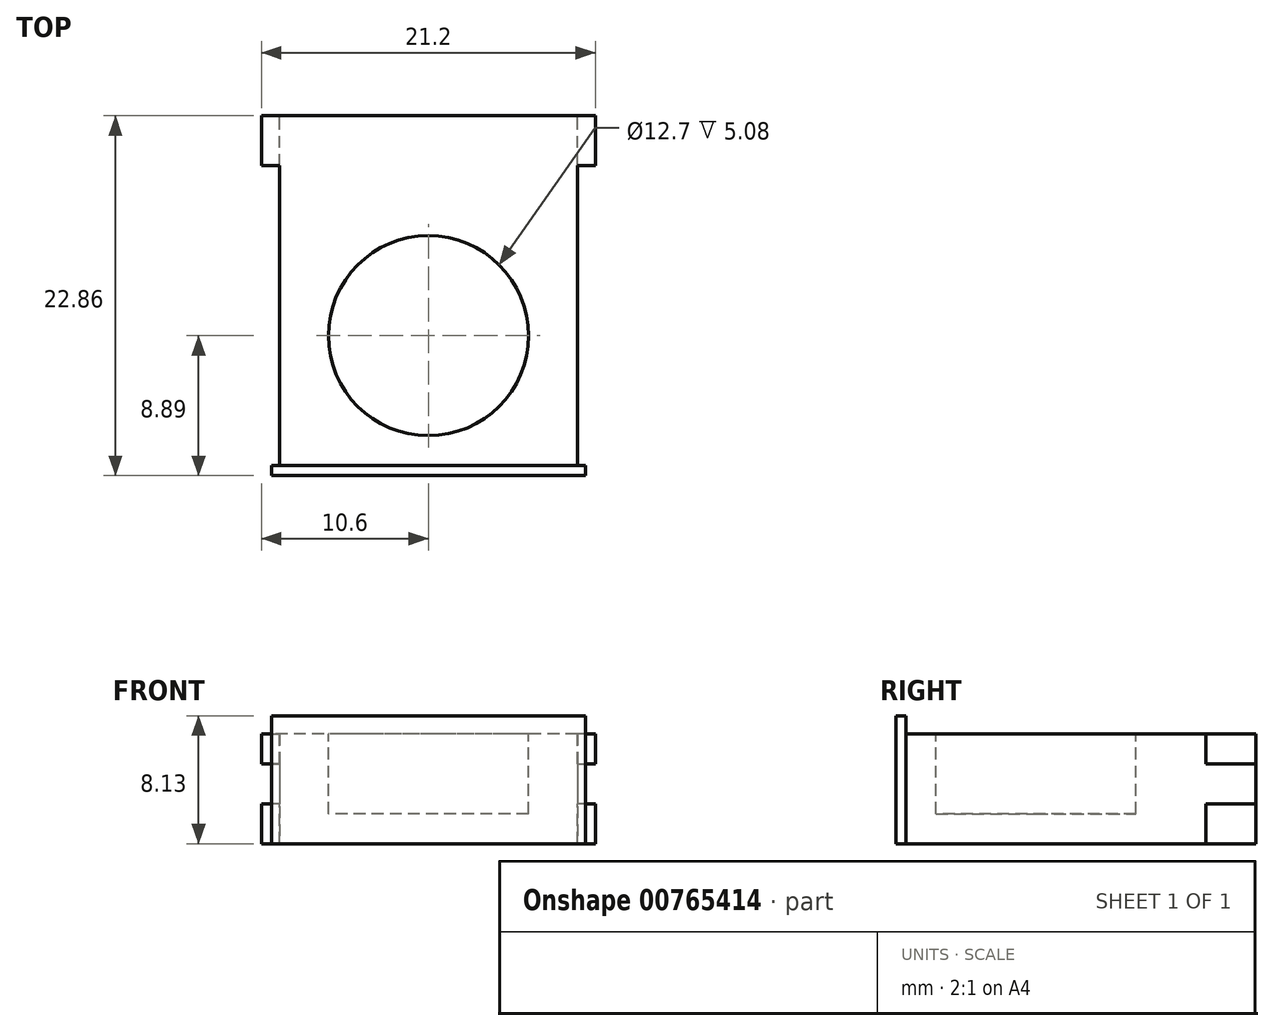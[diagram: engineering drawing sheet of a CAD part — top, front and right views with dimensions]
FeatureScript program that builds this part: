
annotation { "Feature Type Name" : "Feature", "Feature Type Description" : "" }
export const myFeature = defineFeature(function(context is Context, id is Id, definition is map)
    precondition{}
    {
        {
            var Q0;
            Q0=qCreatedBy(makeId("Front.planeOp"),FACE);
            var sketch = newSketch(context, id + "F0", { "sketchPlane" : qUnion([Q0])});
            skLineSegment(sketch, "E0.bottom", {"start": v(9.46, 3.18) * mm, "end": v(-9.46, 3.17) * mm});
            skLineSegment(sketch, "E0.top", {"start": v(9.46, -3.8) * mm, "end": v(-9.46, -3.81) * mm});
            skLineSegment(sketch, "E0.left", {"start": v(9.46, 3.18) * mm, "end": v(9.46, -3.8) * mm});
            skLineSegment(sketch, "E0.right", {"start": v(-9.46, 3.17) * mm, "end": v(-9.46, -3.81) * mm});
            skPoint(sketch, "E0.middle", {"position": v(0, 0) * mm});
            skSolve(sketch);
        }
        {
            var Q0;
            Q0=makeQuery(id+"F0.imprint","IMPRINT",FACE,{"disambiguationData":[TD([[makeQuery(id+"F0.imprint","IMPRINT",EDGE,{"derivedFrom":sQuery(id+"F0.wireOp",EDGE,"E0.bottom")}),1.0]])]});
            extrude(context, id + "F1", {"entities" : qUnion([Q0]), "depth" : 22.86 * mm, "offsetDistance" : 25.4 * mm});
        }
        {
            var Q0;
            Q0=makeQuery(id+"F1.opExtrude","CAP_FACE",FACE,{"disambiguationData":[OSD([sQuery(id+"F0.wireOp",EDGE,"E0.bottom"),sQuery(id+"F0.wireOp",EDGE,"E0.top"),sQuery(id+"F0.wireOp",EDGE,"E0.left"),sQuery(id+"F0.wireOp",EDGE,"E0.right")])],"isStart":false});
            var sketch = newSketch(context, id + "F2", { "sketchPlane" : qUnion([Q0])});
            skLineSegment(sketch, "E1.0", {"start": v(-9.97, 4.32) * mm, "end": v(-9.97, -3.81) * mm});
            skLineSegment(sketch, "E1.1", {"start": v(9.98, 4.32) * mm, "end": v(-9.97, 4.32) * mm});
            skLineSegment(sketch, "E1.2", {"start": v(9.98, 4.32) * mm, "end": v(9.98, -3.8) * mm});
            skLineSegment(sketch, "E1.3", {"start": v(9.98, -3.8) * mm, "end": v(-9.97, -3.81) * mm});
            skSolve(sketch);
        }
        {
            var Q0;
            Q0=makeQuery(id+"F2.imprint","IMPRINT",FACE,{"disambiguationData":[TD([[makeQuery(id+"F2.imprint","IMPRINT",EDGE,{"derivedFrom":sQuery(id+"F2.wireOp",EDGE,"E1.0")}),1.0]])]});
            extrude(context, id + "F3", {"entities" : qUnion([Q0]), "operationType" : NewBodyOperationType.ADD, "oppositeDirection" : true, "depth" : 0.64 * mm, "offsetDistance" : 25.4 * mm});
        }
        {
            var Q0;
            Q0=makeQuery(id+"F1.opExtrude","SWEPT_FACE",FACE,{"disambiguationData":[OSD([sQuery(id+"F0.wireOp",EDGE,"E0.bottom")])]});
            var sketch = newSketch(context, id + "F4", { "sketchPlane" : qUnion([Q0])});
            skPoint(sketch, "E2", {"position": v(0, -13.97) * mm});
            skCircle(sketch, "E3", {"center": v(0, -13.97) * mm, "radius": 6.35 * mm});
            skLineSegment(sketch, "E4", {"start": v(-9.46, 0) * mm, "end": v(-10.6, 0) * mm});
            skLineSegment(sketch, "E5", {"start": v(-10.6, 0) * mm, "end": v(-10.6, -3.17) * mm});
            skLineSegment(sketch, "E6", {"start": v(-10.6, -3.17) * mm, "end": v(-9.46, -3.17) * mm});
            skLineSegment(sketch, "E7.MirrorCS", {"start": v(9.46, 0) * mm, "end": v(10.6, 0) * mm});
            skLineSegment(sketch, "E8.MirrorCS", {"start": v(10.6, 0) * mm, "end": v(10.6, -3.17) * mm});
            skLineSegment(sketch, "E9.MirrorCS", {"start": v(10.6, -3.17) * mm, "end": v(9.46, -3.17) * mm});
            skSolve(sketch);
        }
        {
            var Q0;
            Q0=makeQuery(id+"F4.imprint","IMPRINT",FACE,{"disambiguationData":[TD([[makeQuery(id+"F4.imprint","IMPRINT",EDGE,{"derivedFrom":sQuery(id+"F4.wireOp",EDGE,"E3")}),1.0]])]});
            extrude(context, id + "F5", {"entities" : qUnion([Q0]), "operationType" : NewBodyOperationType.REMOVE, "oppositeDirection" : true, "depth" : 5.08 * mm, "offsetDistance" : 25.4 * mm});
        }
        {
            var Q0;
            {var subQ0=sQuery(id+"F4.wireOp",EDGE,"E4");Q0=makeQuery(id+"F4.imprint","IMPRINT",FACE,{"disambiguationData":[TD([[makeQuery(id+"F4.imprint","IMPRINT",EDGE,{"derivedFrom":subQ0}),1.0]])]});}
            var Q1;
            {var subQ0=sQuery(id+"F4.wireOp",EDGE,"E7.MirrorCS");Q1=makeQuery(id+"F4.imprint","IMPRINT",FACE,{"disambiguationData":[TD([[makeQuery(id+"F4.imprint","IMPRINT",EDGE,{"derivedFrom":subQ0}),-1.0]])]});}
            var Q2;
            {var subQ0=sQuery(id+"F2.wireOp",EDGE,"E1.3");Q2=makeQuery(id+"F3.boolean.opBoolean","MERGE",FACE,{"derivedFrom":[makeQuery(id+"F1.opExtrude","SWEPT_FACE",FACE,{"disambiguationData":[OSD([sQuery(id+"F0.wireOp",EDGE,"E0.top")])]}),makeQuery(id+"F3.opExtrude","SWEPT_FACE",FACE,{"disambiguationData":[OSD([subQ0]),TDD([makeQuery(id+"F2.imprint","IMPRINT",EDGE,{"disambiguationData":[TD([[makeQuery(id+"F2.imprint","INTERSECT",VERTEX,{"derivedFrom":[makeQuery(id+"F1.opExtrude","CAP_EDGE",EDGE,{"disambiguationData":[OSD([sQuery(id+"F0.wireOp",EDGE,"E0.left")])],"isStart":false}),subQ0]}),1.0]])],"derivedFrom":subQ0})])]}),makeQuery(id+"F3.opExtrude","SWEPT_FACE",FACE,{"disambiguationData":[OSD([subQ0]),TDD([makeQuery(id+"F2.imprint","IMPRINT",EDGE,{"disambiguationData":[TD([[makeQuery(id+"F2.imprint","INTERSECT",VERTEX,{"derivedFrom":[makeQuery(id+"F1.opExtrude","CAP_EDGE",EDGE,{"disambiguationData":[OSD([sQuery(id+"F0.wireOp",EDGE,"E0.right")])],"isStart":false}),subQ0]}),-1.0]])],"derivedFrom":subQ0})])]})]});}
            extrude(context, id + "F6", {"entities" : qUnion([Q0, Q1]), "operationType" : NewBodyOperationType.ADD, "endBound" : BoundingType.UP_TO_SURFACE, "oppositeDirection" : true, "depth" : 25.4 * mm, "endBoundEntityFace" : qUnion([Q2]), "offsetDistance" : 25.4 * mm});
        }
        {
            var Q0;
            Q0=makeQuery(id+"F0.imprint","IMPRINT",FACE,{"disambiguationData":[TD([[makeQuery(id+"F0.imprint","IMPRINT",EDGE,{"derivedFrom":sQuery(id+"F0.wireOp",EDGE,"E0.bottom")}),1.0]])]});
            var sketch = newSketch(context, id + "F7", { "sketchPlane" : qUnion([Q0])});
            skLineSegment(sketch, "E10", {"start": v(9.46, 1.27) * mm, "end": v(10.6, 1.27) * mm});
            skLineSegment(sketch, "E11", {"start": v(10.6, 1.27) * mm, "end": v(10.6, -1.27) * mm});
            skLineSegment(sketch, "E12", {"start": v(10.6, -1.27) * mm, "end": v(9.46, -1.27) * mm});
            skLineSegment(sketch, "E13.MirrorCS", {"start": v(-9.46, 1.27) * mm, "end": v(-10.6, 1.27) * mm});
            skLineSegment(sketch, "E14.MirrorCS", {"start": v(-10.6, 1.27) * mm, "end": v(-10.6, -1.27) * mm});
            skLineSegment(sketch, "E15.MirrorCS", {"start": v(-10.6, -1.27) * mm, "end": v(-9.46, -1.27) * mm});
            skLineSegment(sketch, "E16", {"start": v(9.46, 1.27) * mm, "end": v(9.46, -1.27) * mm});
            skLineSegment(sketch, "E17.MirrorCS", {"start": v(-9.46, 1.27) * mm, "end": v(-9.46, -1.27) * mm});
            skSolve(sketch);
        }
        {
            var Q0;
            Q0=makeQuery(id+"F7.imprint","IMPRINT",FACE,{"disambiguationData":[TD([[makeQuery(id+"F7.imprint","IMPRINT",EDGE,{"derivedFrom":sQuery(id+"F7.wireOp",EDGE,"E10")}),-1.0]])]});
            var Q1;
            Q1=makeQuery(id+"F7.imprint","IMPRINT",FACE,{"disambiguationData":[TD([[makeQuery(id+"F7.imprint","IMPRINT",EDGE,{"derivedFrom":sQuery(id+"F7.wireOp",EDGE,"E13.MirrorCS")}),1.0]])]});
            extrude(context, id + "F8", {"entities" : qUnion([Q0, Q1]), "operationType" : NewBodyOperationType.REMOVE, "depth" : 12.7 * mm, "offsetDistance" : 25.4 * mm});
        }
    });
